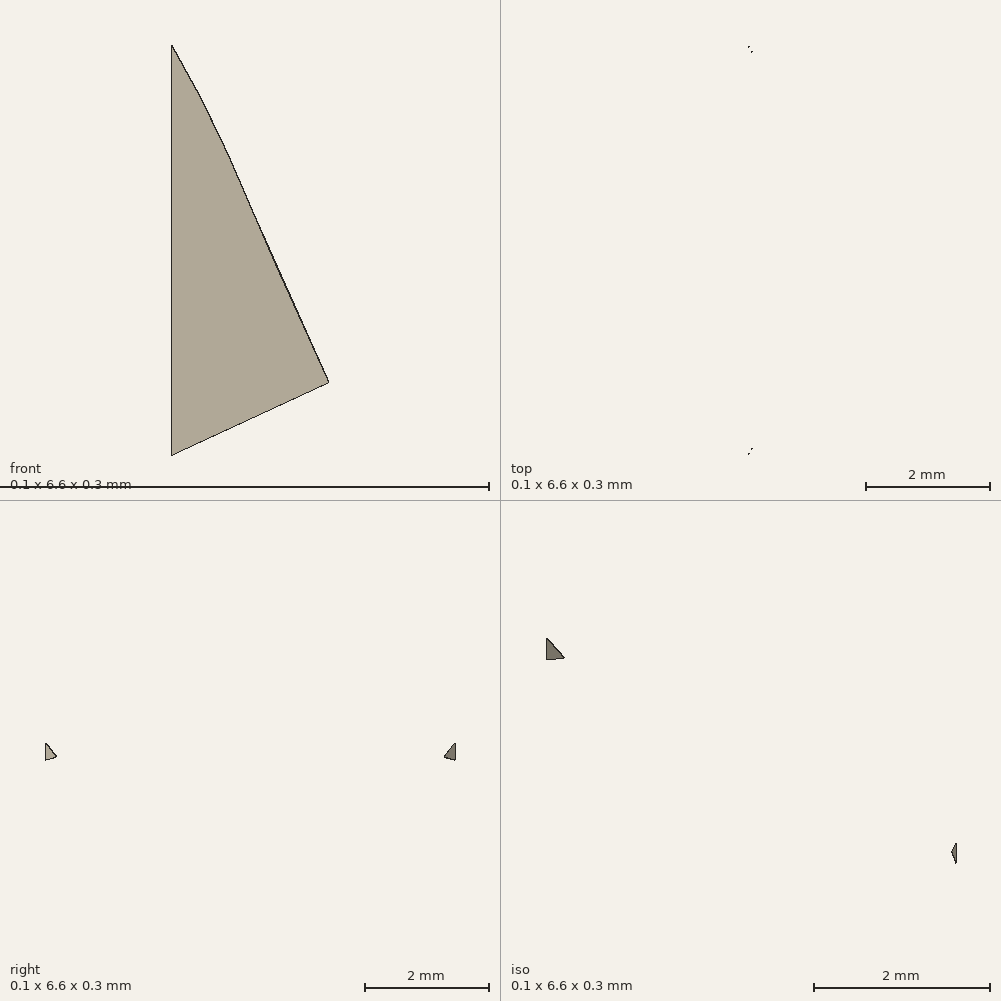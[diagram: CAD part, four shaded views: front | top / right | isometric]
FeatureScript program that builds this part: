
annotation { "Feature Type Name" : "Feature", "Feature Type Description" : "" }
export const myFeature = defineFeature(function(context is Context, id is Id, definition is map)
    precondition{}
    {
        {
            var Q0;
            Q0=qCreatedBy(makeId("Top.planeOp"),FACE);
            var sketch = newSketch(context, id + "F0", { "sketchPlane" : qUnion([Q0])});
            skLineSegment(sketch, "E0.bottom", {"start": v(103.53, -25.15) * mm, "end": v(-103.53, -25.15) * mm});
            skLineSegment(sketch, "E0.top", {"start": v(103.53, 25.15) * mm, "end": v(-103.53, 25.15) * mm});
            skLineSegment(sketch, "E0.left", {"start": v(103.53, -25.15) * mm, "end": v(103.53, 25.15) * mm});
            skLineSegment(sketch, "E0.right", {"start": v(-103.53, -25.15) * mm, "end": v(-103.53, 25.15) * mm});
            skPoint(sketch, "E0.middle", {"position": v(0, 0) * mm});
            skSolve(sketch);
        }
        {
            var Q0;
            Q0=makeQuery(id+"F0.imprint","IMPRINT",FACE,{"disambiguationData":[TD([[makeQuery(id+"F0.imprint","IMPRINT",EDGE,{"derivedFrom":sQuery(id+"F0.wireOp",EDGE,"E0.bottom")}),-1.0]])]});
            extrude(context, id + "F1", {"entities" : qUnion([Q0]), "endBound" : BoundingType.SYMMETRIC, "depth" : 50.8 * mm});
        }
        {
            var Q0;
            Q0=makeQuery(id+"F1.opExtrude","CAP_FACE",FACE,{"disambiguationData":[OSD([sQuery(id+"F0.wireOp",EDGE,"E0.bottom"),sQuery(id+"F0.wireOp",EDGE,"E0.top"),sQuery(id+"F0.wireOp",EDGE,"E0.left"),sQuery(id+"F0.wireOp",EDGE,"E0.right")])],"isStart":false});
            var sketch = newSketch(context, id + "F2", { "sketchPlane" : qUnion([Q0])});
            skFitSpline(sketch, "E1", {"points": [v(96.83, 0) * mm, v(92.01, 7.72) * mm, v(88.87, 8.55) * mm, v(-28.8, 2.06) * mm, v(-30.68, 3.11) * mm, v(-33, 9.31) * mm, v(-36.53, 11.43) * mm, v(-75.7, 9.81) * mm, v(-44.5, 7.5) * mm, v(-75.06, 3.11) * mm], "startDerivative": vector(-75.1, 124.39) * mm, "endDerivative": vector(-371.64, -30.61) * mm});
            skFitSpline(sketch, "E2", {"points": [v(-75.06, 3.11) * mm, v(-75.06, 2.58) * mm, v(-43.3, 0.62) * mm, v(-43.17, 0) * mm], "startDerivative": vector(-4.06, -5.49) * mm, "endDerivative": vector(3.76, 0) * mm});
            skFitSpline(sketch, "E3.MirrorCS", {"points": [v(96.83, 0) * mm, v(92.01, -7.72) * mm, v(88.87, -8.55) * mm, v(-28.8, -2.06) * mm, v(-30.68, -3.11) * mm, v(-33, -9.31) * mm, v(-36.53, -11.43) * mm, v(-75.7, -9.81) * mm, v(-44.5, -7.5) * mm, v(-75.06, -3.11) * mm], "startDerivative": vector(-75.1, -124.39) * mm, "endDerivative": vector(-371.64, 30.61) * mm});
            skFitSpline(sketch, "E4.MirrorCS", {"points": [v(-75.06, -3.11) * mm, v(-75.06, -2.58) * mm, v(-43.3, -0.62) * mm, v(-43.17, 0) * mm], "startDerivative": vector(-4.06, 5.49) * mm, "endDerivative": vector(3.76, 0) * mm});
            skArc(sketch, "E5.filletArc", {"start": v(94.82, -3.3) * mm, "mid": v(95.75, 0) * mm, "end": v(94.82, 3.3) * mm});
            skSolve(sketch);
        }
        {
            var Q0;
            Q0=makeQuery(id+"F2.imprint","IMPRINT",FACE,{"disambiguationData":[TD([[makeQuery(id+"F2.imprint","IMPRINT",EDGE,{"derivedFrom":sQuery(id+"F2.wireOp",EDGE,"E1")}),1.0]])]});
            var Q1;
            Q1 = qSketchRegion(id + "F4", true);
            extrude(context, id + "F3", {"entities" : qUnion([Q0, Q1]), "operationType" : NewBodyOperationType.INTERSECT, "endBound" : BoundingType.SYMMETRIC, "depth" : 50.8 * mm});
        }
        {
            var Q0;
            Q0=qCreatedBy(makeId("Front.planeOp"),FACE);
            var sketch = newSketch(context, id + "F4", { "sketchPlane" : qUnion([Q0])});
            skSolve(sketch);
        }
        {
            var Q0;
            Q0=qCreatedBy(makeId("Front.planeOp"),FACE);
            var sketch = newSketch(context, id + "F5", { "sketchPlane" : qUnion([Q0])});
            skFitSpline(sketch, "E6", {"points": [v(-74.66, 14.17) * mm, v(-50.4, 11.79) * mm, v(-29.12, 13.57) * mm, v(13.44, 11.98) * mm, v(73.9, 13.38) * mm, v(93.38, 15.17) * mm, v(93.78, 14.77) * mm], "startDerivative": vector(147.7, -22.15) * mm, "endDerivative": vector(8.12, -17.56) * mm});
            skFitSpline(sketch, "E7.0", {"points": [v(-74.47, 15.43) * mm, v(-72.93, 15.2) * mm, v(-69.86, 14.74) * mm, v(-65.3, 14.1) * mm, v(-60.8, 13.56) * mm, v(-56.43, 13.18) * mm, v(-52.9, 13.04) * mm, v(-50.17, 13.05) * mm, v(-47.5, 13.15) * mm, v(-44.2, 13.41) * mm, v(-40.22, 13.86) * mm, v(-36.1, 14.33) * mm, v(-32.45, 14.66) * mm, v(-29.35, 14.85) * mm, v(-26.13, 14.95) * mm, v(-21.88, 14.95) * mm, v(-16.44, 14.8) * mm, v(-10.67, 14.52) * mm, v(-4.6, 14.17) * mm, v(1.79, 13.8) * mm, v(8.44, 13.45) * mm, v(15.36, 13.17) * mm, v(22.51, 12.98) * mm, v(32.25, 12.86) * mm, v(42.11, 12.94) * mm, v(51.77, 13.22) * mm, v(58.82, 13.53) * mm, v(65.6, 13.94) * mm, v(70.95, 14.36) * mm, v(75, 14.76) * mm, v(77.93, 15.08) * mm, v(80.7, 15.4) * mm, v(83.28, 15.7) * mm, v(85.64, 16) * mm, v(87.77, 16.24) * mm, v(89.32, 16.4) * mm, v(90.4, 16.49) * mm, v(91.16, 16.54) * mm, v(91.83, 16.57) * mm, v(92.43, 16.57) * mm, v(92.87, 16.55) * mm, v(93.21, 16.5) * mm, v(93.46, 16.46) * mm, v(93.71, 16.4) * mm, v(93.99, 16.3) * mm, v(94.25, 16.15) * mm, v(94.49, 15.96) * mm, v(94.68, 15.75) * mm, v(94.85, 15.48) * mm, v(94.91, 15.35) * mm, v(94.93, 15.3) * mm]});
            skFitSpline(sketch, "E8", {"points": [v(93.78, 14.77) * mm, v(94.93, 15.3) * mm], "startDerivative": vector(1.15, 0.53) * mm, "endDerivative": vector(1.15, 0.53) * mm});
            skFitSpline(sketch, "E9", {"points": [v(-74.66, 14.17) * mm, v(-75.12, 14.77) * mm, v(-74.47, 15.43) * mm], "startDerivative": vector(-1.51, 1.26) * mm, "endDerivative": vector(1.83, 1.25) * mm});
            skSolve(sketch);
        }
        {
            var Q0;
            Q0=qSketchRegion(id+"F5",true);
            extrude(context, id + "F6", {"entities" : qUnion([Q0]), "operationType" : NewBodyOperationType.INTERSECT, "endBound" : BoundingType.SYMMETRIC, "depth" : 25.4 * mm});
        }
    });
